# Revit family: Haworth_Janus_Slant_ThreeSeatSofa
name_source: partatom
category: Furniture
revit_build: Autodesk Revit 2018 (Build: 20170223_1515(x64)
units: mm (PartAtom-declared; Revit-internal decimal feet)

## family parameters
Always vertical = Yes
Cut with Voids When Loaded = No
OmniClass Number = 23.40.20.00
OmniClass Title = General Furniture and Specialties
Room Calculation Point = No
Shared = No
Work Plane-Based = No

## types (1)
- HCJC-SL-L3
    Assembly Code = E2020200
    Cushion = Yes
    Depth = 31 in.
    Description = Haworth - Janus - Slant - Three Seat Sofa
    Frame = Yes
    Height = 30.25 in.
    Manufacturer = Haworth
    Model = HCJC-SL-L3
    Revision = 2
    Size = Verify Final Dim. w/ Haworth
    URL = http://www.haworth.com
    URL - Product = https://www.haworth.com
    Warranty = https://www.haworth.com
    Width = 85.5 in.
    With Seat Cushion = Yes

## geometry (parser evidence)
native form markers: Sweep x8
no freeform markers — native parametric forms only
